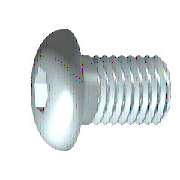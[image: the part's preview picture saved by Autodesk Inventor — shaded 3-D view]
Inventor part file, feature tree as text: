
AUTODESK INVENTOR PART (.ipt)
format: ipt  version: 2025 (Build 290162010, 162A)  size: 191,488 bytes
history: native  units: mm (DEFAULTED — no unit token found)
features: extrude x1, plane x1, fillet x1
ambient origin geometry x7: Origin, YZ Plane, XY Plane, X Axis, Y Axis, Z Axis, Center Point
bodies: Solid1 (feature_tree), Body (feature_tree)
feature tree (3):
  extrude  "Slot"  Depth=18.5mm
  plane  "Work Plane1"
  fillet  "Fillet2"  Radius=0.306825mm
